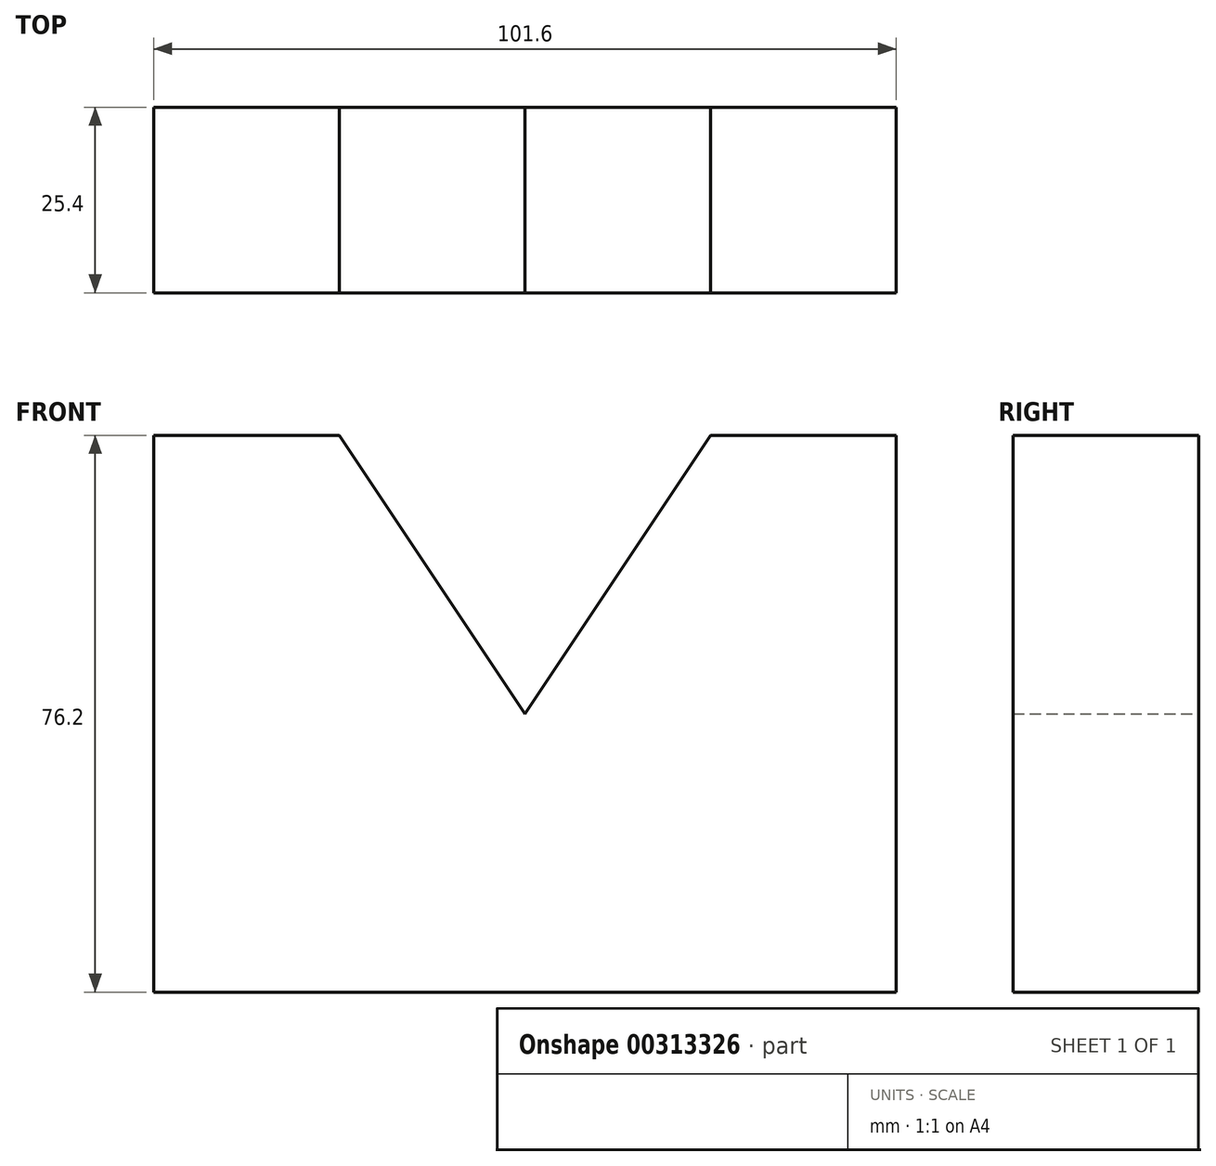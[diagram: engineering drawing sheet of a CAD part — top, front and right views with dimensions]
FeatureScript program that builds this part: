
annotation { "Feature Type Name" : "Feature", "Feature Type Description" : "" }
export const myFeature = defineFeature(function(context is Context, id is Id, definition is map)
    precondition{}
    {
        {
            var Q0;
            Q0=qCreatedBy(makeId("Front.planeOp"),FACE);
            var sketch = newSketch(context, id + "F0", { "sketchPlane" : qUnion([Q0])});
            skLineSegment(sketch, "E0", {"start": v(-63.5, 31.48) * mm, "end": v(-63.5, -44.72) * mm});
            skLineSegment(sketch, "E1", {"start": v(-63.5, 31.48) * mm, "end": v(-38.1, 31.48) * mm});
            skLineSegment(sketch, "E2", {"start": v(-63.5, -44.72) * mm, "end": v(38.1, -44.72) * mm});
            skLineSegment(sketch, "E3", {"start": v(38.1, -44.72) * mm, "end": v(38.1, 31.48) * mm});
            skLineSegment(sketch, "E4", {"start": v(38.1, 31.48) * mm, "end": v(12.7, 31.48) * mm});
            skLineSegment(sketch, "E5", {"start": v(-38.1, 31.48) * mm, "end": v(-12.7, -6.62) * mm});
            skLineSegment(sketch, "E6", {"start": v(12.7, 31.48) * mm, "end": v(-12.7, -6.62) * mm});
            skSolve(sketch);
        }
        {
            var Q0;
            Q0=makeQuery(id+"F0.imprint","IMPRINT",FACE,{"disambiguationData":[TD([[makeQuery(id+"F0.imprint","IMPRINT",EDGE,{"derivedFrom":sQuery(id+"F0.wireOp",EDGE,"E0")}),1.0]])]});
            extrude(context, id + "F1", {"entities" : qUnion([Q0]), "depth" : 25.4 * mm});
        }
    });
